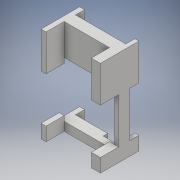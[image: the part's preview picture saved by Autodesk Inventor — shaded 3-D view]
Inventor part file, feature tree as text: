
AUTODESK INVENTOR PART (.ipt)
format: ipt  version: 2017 (Build 210142000, 142)  size: 348,160 bytes
history: native  units: mm
features: sketch x21, extrude x20
ambient origin geometry x8: Origin, YZ Plane, XZ Plane, XY Plane, X Axis, Y Axis, Z Axis, Center Point
bodies: Solid1 (feature_tree)
feature tree (41):
  sketch  "Sketch1"  dims[d0=160.0mm d1=210.0mm]
  extrude  "Extrusion1"  Depth=210.0mm
  extrude  "Extrusion2"  Depth=9.0mm
  extrude  "Extrusion3"  Depth=122.0mm
  extrude  "Extrusion4"  Depth=29.0mm TaperAngle=0.0deg
  extrude  "Extrusion5"  Depth=11.0mm
  extrude  "Extrusion6"  Depth=11.0mm
  sketch  "Sketch8"  dims[d18=20.0mm d19=0.0mm d20=100.0mm]
  extrude  "Extrusion7"  Depth=100.0mm
  extrude  "Extrusion8"  Depth=100.0mm
  extrude  "Extrusion9"  Depth=100.0mm
  extrude  "Extrusion10"  Depth=20.0mm TaperAngle=0.0deg
  extrude  "Extrusion11"  Depth=100.0mm
  sketch  "Sketch14"  dims[d34=10.0mm d35=0.0mm d36=11.0mm d37=0.0mm]
  sketch  "Sketch15"  dims[d38=111.0mm d39=10.0mm]
  extrude  "Extrusion12"  Depth=9.0mm
  extrude  "Extrusion13"  Depth=11.0mm TaperAngle=0.0deg
  extrude  "Extrusion14"  Depth=10.0mm
  extrude  "Extrusion15"  Depth=25.0mm
  extrude  "Extrusion16"  Depth=100.0mm TaperAngle=0.0deg
  extrude  "Extrusion17"  Depth=9.0mm TaperAngle=0.0deg
  extrude  "Extrusion18"  Depth=10.0mm TaperAngle=0.0deg
  extrude  "Extrusion19"  Depth=10.0mm TaperAngle=0.0deg
  extrude  "Extrusion20"  Depth=19.0mm
  sketch  "Sketch2"  dims[d2=55.0mm d3=0.0mm d4=9.0mm]
  sketch  "Sketch3"  dims[d5=10.0mm d6=122.0mm]
  sketch  "Sketch4"  dims[d7=122.0mm d8=0.0mm d9=29.0mm d10=0.0mm]
  sketch  "Sketch5"  dims[d11=25.0mm d12=0.0mm d13=11.0mm]
  sketch  "Sketch6"  dims[d14=11.0mm d15=11.0mm]
  sketch  "Sketch7"  dims[d16=11.0mm d17=100.0mm]
  sketch  "Sketch10"  dims[d21=100.0mm d22=100.0mm]
  sketch  "Sketch11"  dims[d23=11.0mm d24=20.0mm d25=0.0mm]
  sketch  "Sketch12"  dims[d26=20.0mm d27=100.0mm]
  sketch  "Sketch13"  dims[d28=9.0mm d29=110.0mm]
  sketch  "Sketch16"  dims[d40=80.0mm d41=0.0mm d42=25.0mm]
  sketch  "Sketch18"  dims[d43=100.0mm d44=220.0mm d45=0.0mm]
  sketch  "Sketch19"  dims[d46=100.0mm d47=9.0mm d48=0.0mm]
  sketch  "Sketch20"  dims[d49=10.0mm d50=0.0mm d51=10.0mm d52=0.0mm]
  sketch  "Sketch21"  dims[d53=10.0mm d54=0.0mm d55=10.0mm d56=0.0mm]
  sketch  "Sketch22"  dims[d57=11.0mm d58=0.0mm d59=19.0mm]
  sketch  "Sketch23"  dims[d60=10.0mm d61=19.0mm d62=0.0mm d63=10.0mm d64=0.0mm d65=20.0mm d66=0.0mm d67=10.0mm d68=0.0mm]
